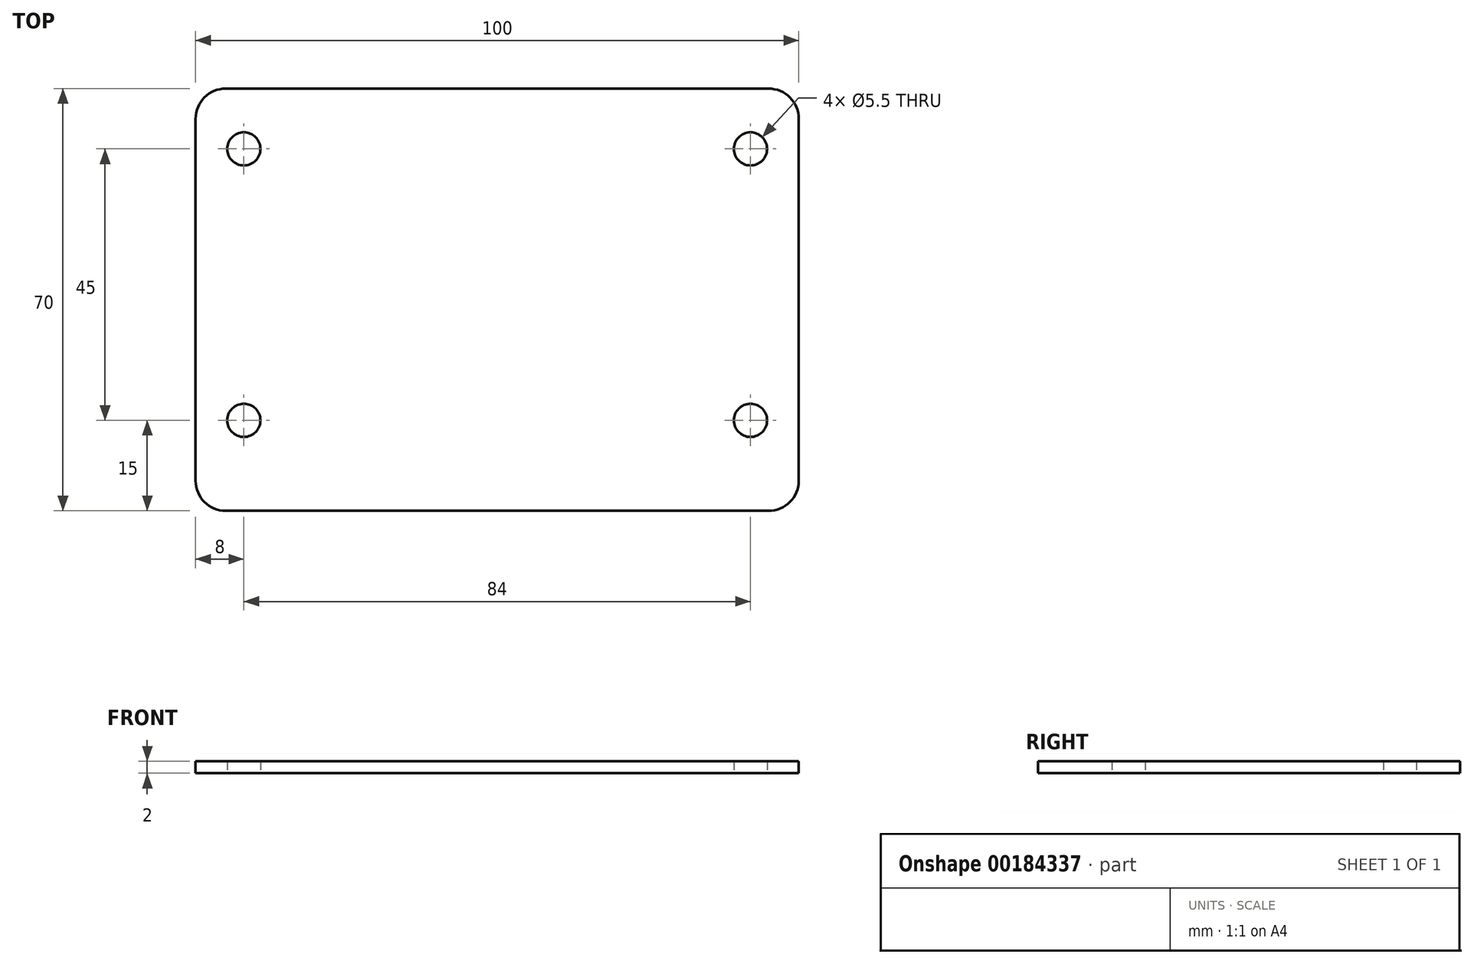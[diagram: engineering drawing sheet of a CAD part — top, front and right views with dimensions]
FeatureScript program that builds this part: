
annotation { "Feature Type Name" : "Feature", "Feature Type Description" : "" }
export const myFeature = defineFeature(function(context is Context, id is Id, definition is map)
    precondition{}
    {
        {
            var Q0;
            Q0=qCreatedBy(makeId("Top.planeOp"),FACE);
            var sketch = newSketch(context, id + "F0", { "sketchPlane" : qUnion([Q0])});
            skLineSegment(sketch, "E0.bottom", {"start": v(45, 35) * mm, "end": v(-45, 35) * mm});
            skLineSegment(sketch, "E0.top", {"start": v(45, -35) * mm, "end": v(-45, -35) * mm});
            skLineSegment(sketch, "E0.left", {"start": v(50, 30) * mm, "end": v(50, -30) * mm});
            skLineSegment(sketch, "E0.right", {"start": v(-50, 30) * mm, "end": v(-50, -30) * mm});
            skPoint(sketch, "E0.middle", {"position": v(0, 0) * mm});
            skPoint(sketch, "E1.visualSharp", {"position": v(-50, 35) * mm});
            skArc(sketch, "E1.filletArc", {"start": v(-45, 35) * mm, "mid": v(-48.54, 33.54) * mm, "end": v(-50, 30) * mm});
            skPoint(sketch, "E2.visualSharp", {"position": v(50, -35) * mm});
            skArc(sketch, "E2.filletArc", {"start": v(45, -35) * mm, "mid": v(48.54, -33.54) * mm, "end": v(50, -30) * mm});
            skPoint(sketch, "E3.visualSharp", {"position": v(50, 35) * mm});
            skArc(sketch, "E3.filletArc", {"start": v(50, 30) * mm, "mid": v(48.54, 33.54) * mm, "end": v(45, 35) * mm});
            skPoint(sketch, "E4.visualSharp", {"position": v(-50, -35) * mm});
            skArc(sketch, "E4.filletArc", {"start": v(-50, -30) * mm, "mid": v(-48.54, -33.54) * mm, "end": v(-45, -35) * mm});
            skCircle(sketch, "E5", {"center": v(-42, -20) * mm, "radius": 2.75 * mm});
            skCircle(sketch, "E6.0.1.0", {"center": v(-42, 25) * mm, "radius": 2.75 * mm});
            skCircle(sketch, "E6.1.0.0", {"center": v(42, -20) * mm, "radius": 2.75 * mm});
            skCircle(sketch, "E6.1.1.0", {"center": v(42, 25) * mm, "radius": 2.75 * mm});
            skLineSegment(sketch, "E6.direction1", {"start": v(-42, -20) * mm, "end": v(42, -20) * mm, "construction": true});
            skLineSegment(sketch, "E6.direction2", {"start": v(-42, -20) * mm, "end": v(-42, 25) * mm, "construction": true});
            skSolve(sketch);
        }
        {
            var Q0;
            Q0=makeQuery(id+"F0.imprint","IMPRINT",FACE,{"disambiguationData":[TD([[makeQuery(id+"F0.imprint","IMPRINT",EDGE,{"derivedFrom":sQuery(id+"F0.wireOp",EDGE,"E0.bottom")}),1.0]])]});
            extrude(context, id + "F1", {"entities" : qUnion([Q0]), "depth" : 2 * mm});
        }
    });
